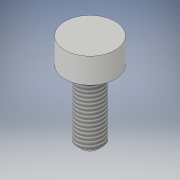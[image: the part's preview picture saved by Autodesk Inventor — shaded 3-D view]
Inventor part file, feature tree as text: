
AUTODESK INVENTOR PART (.ipt)
format: ipt  version: 2018 (Build 220112000, 112)  size: 110,080 bytes
history: native  units: in
note: dims shown in document units (in); Inventor stores cm internally (conversion verified against a paired STEP export)
features: revolve x1, chamfer x1, thread x1, sketch x1
ambient origin geometry x8: Origin, YZ Plane, XZ Plane, XY Plane, X Axis, Y Axis, Z Axis, Center Point
bodies: Solid1 (feature_tree)
feature tree (4):
  revolve  "Revolution1"  [1 undecoded]
  chamfer  "Chamfer1"  Distance=0.4724in
  thread  "Thread1"  [1 undecoded]
  sketch  "Sketch2"  dims[d3=1.7717in d6=0.4724in d7=0.4724in d8=0.2362in d9=90.0deg d10=0.0787in d11=0.0787in d12=45.0deg d13=0.3937in d14=0.0in]
note: 2 required parameter values undecoded (feature->parameter linkage not recoverable at this tier; creation-order binding heuristic only, values carry confidence <= 0.55)